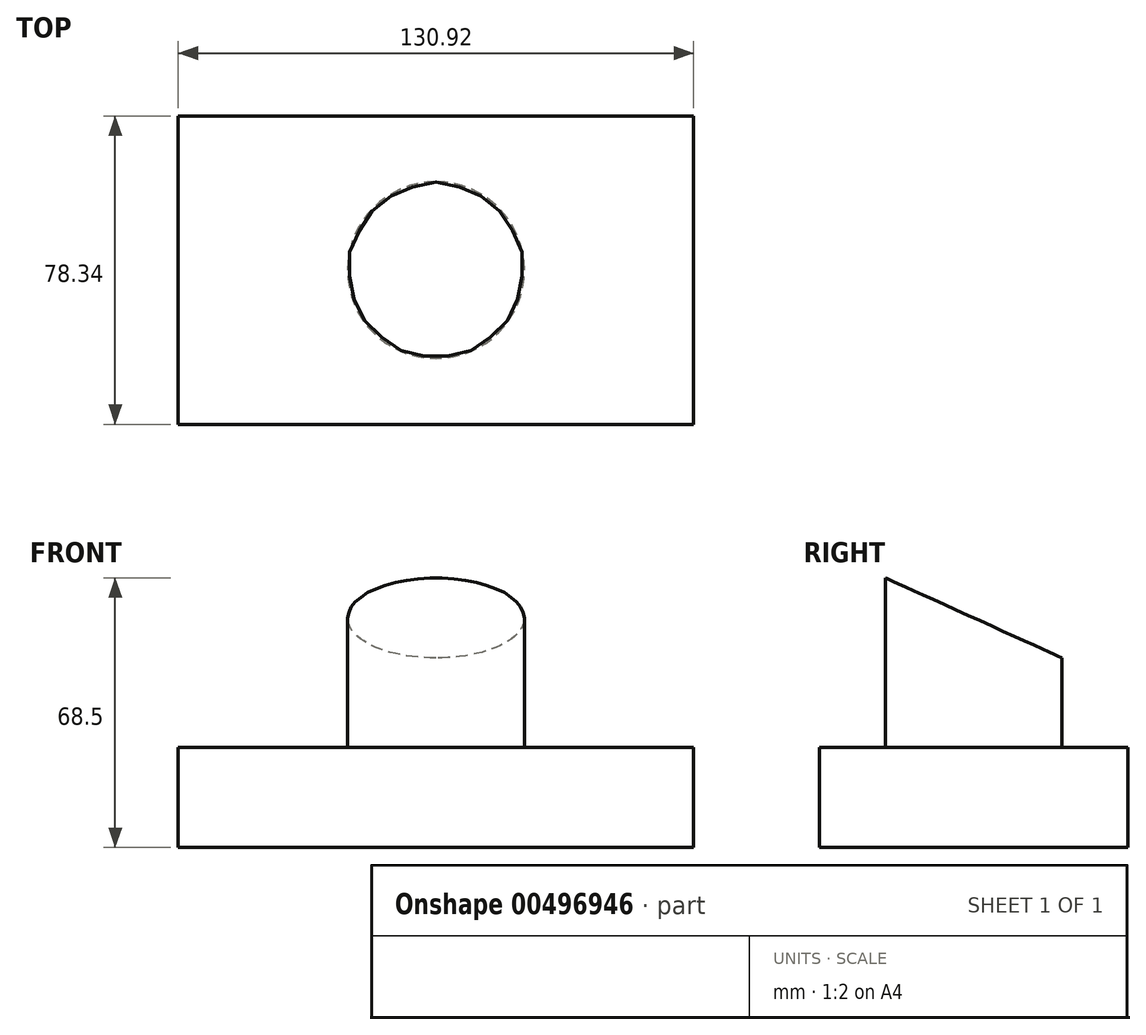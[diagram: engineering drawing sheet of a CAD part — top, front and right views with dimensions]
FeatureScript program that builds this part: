
annotation { "Feature Type Name" : "Feature", "Feature Type Description" : "" }
export const myFeature = defineFeature(function(context is Context, id is Id, definition is map)
    precondition{}
    {
        {
            var Q0;
            Q0=qCreatedBy(makeId("Top.planeOp"),FACE);
            var sketch = newSketch(context, id + "F0", { "sketchPlane" : qUnion([Q0])});
            skLineSegment(sketch, "E0.bottom", {"start": v(65.46, 39.17) * mm, "end": v(-65.46, 39.17) * mm});
            skLineSegment(sketch, "E0.top", {"start": v(65.46, -39.17) * mm, "end": v(-65.46, -39.17) * mm});
            skLineSegment(sketch, "E0.left", {"start": v(65.46, 39.17) * mm, "end": v(65.46, -39.17) * mm});
            skLineSegment(sketch, "E0.right", {"start": v(-65.46, 39.17) * mm, "end": v(-65.46, -39.17) * mm});
            skPoint(sketch, "E0.middle", {"position": v(0, 0) * mm});
            skSolve(sketch);
        }
        {
            var Q0;
            Q0 = qSketchRegion(id + "F0", true);
            extrude(context, id + "F1", {"entities" : qUnion([Q0]), "depth" : 25.4 * mm});
        }
        {
            var Q0;
            Q0=makeQuery(id+"F1.opExtrude","CAP_FACE",FACE,{"disambiguationData":[OSD([sQuery(id+"F0.wireOp",EDGE,"E0.bottom"),sQuery(id+"F0.wireOp",EDGE,"E0.top"),sQuery(id+"F0.wireOp",EDGE,"E0.left"),sQuery(id+"F0.wireOp",EDGE,"E0.right")])],"isStart":false});
            var sketch = newSketch(context, id + "F2", { "sketchPlane" : qUnion([Q0])});
            skCircle(sketch, "E1", {"center": v(0, 0) * mm, "radius": 22.45 * mm});
            skSolve(sketch);
        }
        {
            var Q0;
            Q0=makeQuery(id+"F2.imprint","IMPRINT",FACE,{"disambiguationData":[TD([[makeQuery(id+"F2.imprint","IMPRINT",EDGE,{"derivedFrom":sQuery(id+"F2.wireOp",EDGE,"E1")}),1.0]])]});
            extrude(context, id + "F3", {"entities" : qUnion([Q0]), "operationType" : NewBodyOperationType.ADD, "depth" : 45.47 * mm});
        }
        {
            var Q0;
            Q0=qCreatedBy(makeId("Right.planeOp"),FACE);
            var sketch = newSketch(context, id + "F4", { "sketchPlane" : qUnion([Q0])});
            skLineSegment(sketch, "E2", {"start": v(-29.93, 71.9) * mm, "end": v(39.73, 40.28) * mm});
            skLineSegment(sketch, "E3", {"start": v(39.73, 40.28) * mm, "end": v(39.73, 72.18) * mm});
            skLineSegment(sketch, "E4", {"start": v(39.73, 72.18) * mm, "end": v(-29.93, 71.9) * mm});
            skSolve(sketch);
        }
        {
            var Q0;
            Q0=makeQuery(id+"F4.imprint","IMPRINT",FACE,{"disambiguationData":[TD([[makeQuery(id+"F4.imprint","IMPRINT",EDGE,{"derivedFrom":sQuery(id+"F4.wireOp",EDGE,"E2")}),1.0]])]});
            extrude(context, id + "F5", {"entities" : qUnion([Q0]), "operationType" : NewBodyOperationType.REMOVE, "depth" : 76.2 * mm, "symmetric" : true});
        }
    });
